# Revit family: AFX-Twist-Pendant+
name_source: partatom
category: Lighting Fixtures
units: mm (PartAtom-declared; Revit-internal decimal feet)

## family parameters
Cut with Voids When Loaded = No
Host = Face
Light Source = Yes
Part Type = Normal
Room Calculation Point = No
Round Connector Dimension = Use Diameter
Shared = No

## types (1)
- TWTP48
    Apparent Load = 0 VA
    Assembly Code = D5020200
    Body Finish = AFX - Powder Coated, Black
    Cable Finish = AFX - Stainless Steel
    Color Filter = 16777215
    Color Rendering Index = 90
    Default Elevation = 48"
    Description = 48'' LED Pendant
    Dimming Lamp Color Temperature Shift = <None>
    Emit from Line Length = 24"
    Height = 1 5/8"
    Lamp = LED
    Length = 47 1/4"
    Manufacturer = AFX Inc
    Model = TWTP48
    Photometric Web File = TWTP48L30D1xx_IES.IES
    Product Documentation Link = https://www.afxinc.com
    Revit Model Built By = https://servex-us.com
    Screen Finish = AFX - Diffuser
    Tilt Angle = 90.00°
    Type Comments = TWIST
    URL = https://www.afxinc.com
    Voltage = 120 V
    Wattage Comments = 40W
    Width = 11 3/4"

## geometry (parser evidence)
native form markers: Sweep x4
no freeform markers — native parametric forms only
